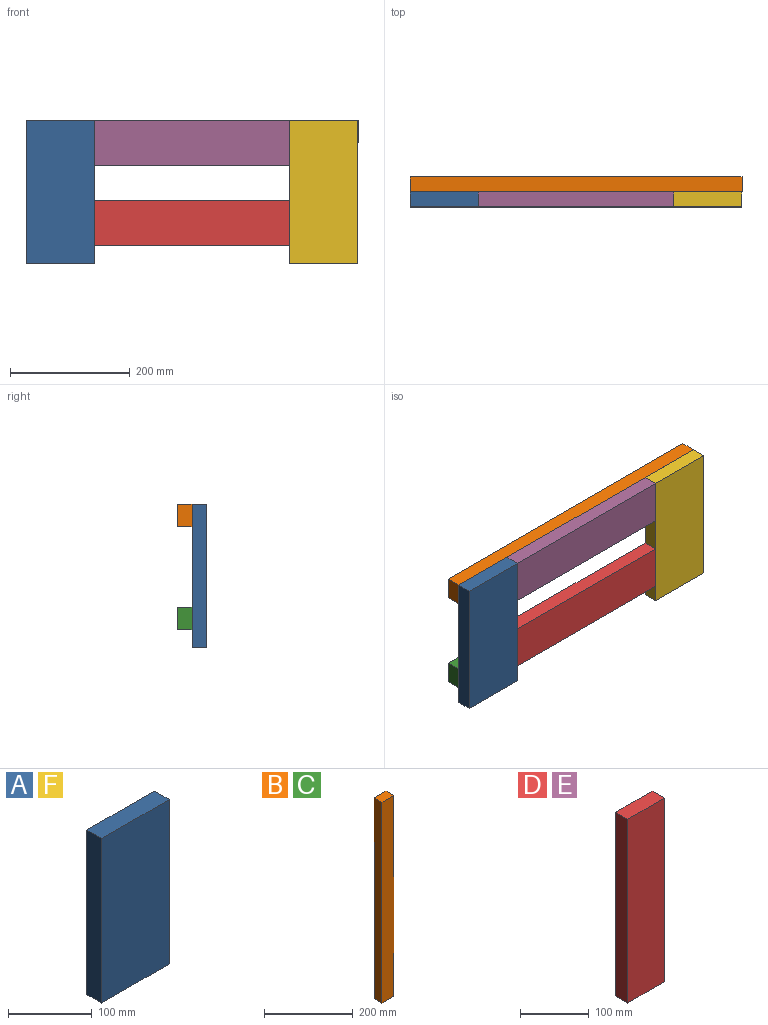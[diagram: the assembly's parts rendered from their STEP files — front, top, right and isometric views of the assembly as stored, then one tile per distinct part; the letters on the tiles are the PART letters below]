
ASSEMBLY  parts=6 mates=5
PART A: 6 faces, bbox 114x25x240 mm
  f0: plane 114x25mm, normal (0,0,1), area 2850mm2, adj f1,f3,f4,f5
  f1: plane 240x25mm, normal (-1,0,0), area 6000mm2, adj f0,f2,f4,f5
  f2: plane 114x25mm, normal (0,0,-1), area 2850mm2, adj f1,f3,f4,f5
  f3: plane 240x25mm, normal (1,0,0), area 6000mm2, adj f0,f2,f4,f5
  f4: plane 240x114mm, normal (0,-1,0), area 27360mm2, adj f0,f1,f2,f3
  f5: plane 240x114mm, normal (0,1,0), area 27360mm2, adj f0,f1,f2,f3
PART B: 6 faces, bbox 38x25x555 mm
  f0: plane 38x25mm, normal (0,0,1), area 950mm2, adj f1,f3,f4,f5
  f1: plane 555x25mm, normal (-1,0,0), area 13875mm2, adj f0,f2,f4,f5
  f2: plane 38x25mm, normal (0,0,-1), area 950mm2, adj f1,f3,f4,f5
  f3: plane 555x25mm, normal (1,0,0), area 13875mm2, adj f0,f2,f4,f5
  f4: plane 555x38mm, normal (0,-1,0), area 21090mm2, adj f0,f1,f2,f3
  f5: plane 555x38mm, normal (0,1,0), area 21090mm2, adj f0,f1,f2,f3
PART C: same geometry as B
PART D: 6 faces, bbox 76x25x327 mm
  f0: plane 76x25mm, normal (0,0,1), area 1900mm2, adj f1,f3,f4,f5
  f1: plane 327x25mm, normal (-1,0,0), area 8175mm2, adj f0,f2,f4,f5
  f2: plane 76x25mm, normal (0,0,-1), area 1900mm2, adj f1,f3,f4,f5
  f3: plane 327x25mm, normal (1,0,0), area 8175mm2, adj f0,f2,f4,f5
  f4: plane 327x76mm, normal (0,-1,0), area 24852mm2, adj f0,f1,f2,f3
  f5: plane 327x76mm, normal (0,1,0), area 24852mm2, adj f0,f1,f2,f3
PART E: same geometry as D
PART F: same geometry as A
PLACE A t=(-2418.35,-431.22,686.52)mm
PLACE B rot(axis=(0.71,0,-0.71),180deg) t=(200.54,-431.22,42.34)mm
PLACE C rot(axis=(0.71,0,-0.71),180deg) t=(200.54,-431.22,-129.66)mm
PLACE D rot(axis=(0,-1,0),90deg) t=(-820.77,-431.22,-121.03)mm
PLACE E rot(axis=(0,-1,0),90deg) t=(-820.77,-431.22,12.97)mm
PLACE F t=(-1977.35,-431.22,686.52)mm
MATE fastened E.f0 <-> A.f3  axis (-1,0,0) through (-386.91,-431.22,12.99)mm
MATE fastened B.f5 <-> E.f5  axis (0,-1,0) through (-223.41,-431.22,12.99)mm
MATE fastened C.f5 <-> D.f5  axis (0,-1,0) through (-223.41,-431.22,-197.01)mm
MATE fastened F.f1 <-> E.f2  axis (-1,0,0) through (-59.91,-443.72,12.99)mm
MATE fastened D.f0 <-> A.f3  axis (-1,0,0) through (-386.91,-431.22,-197.01)mm
